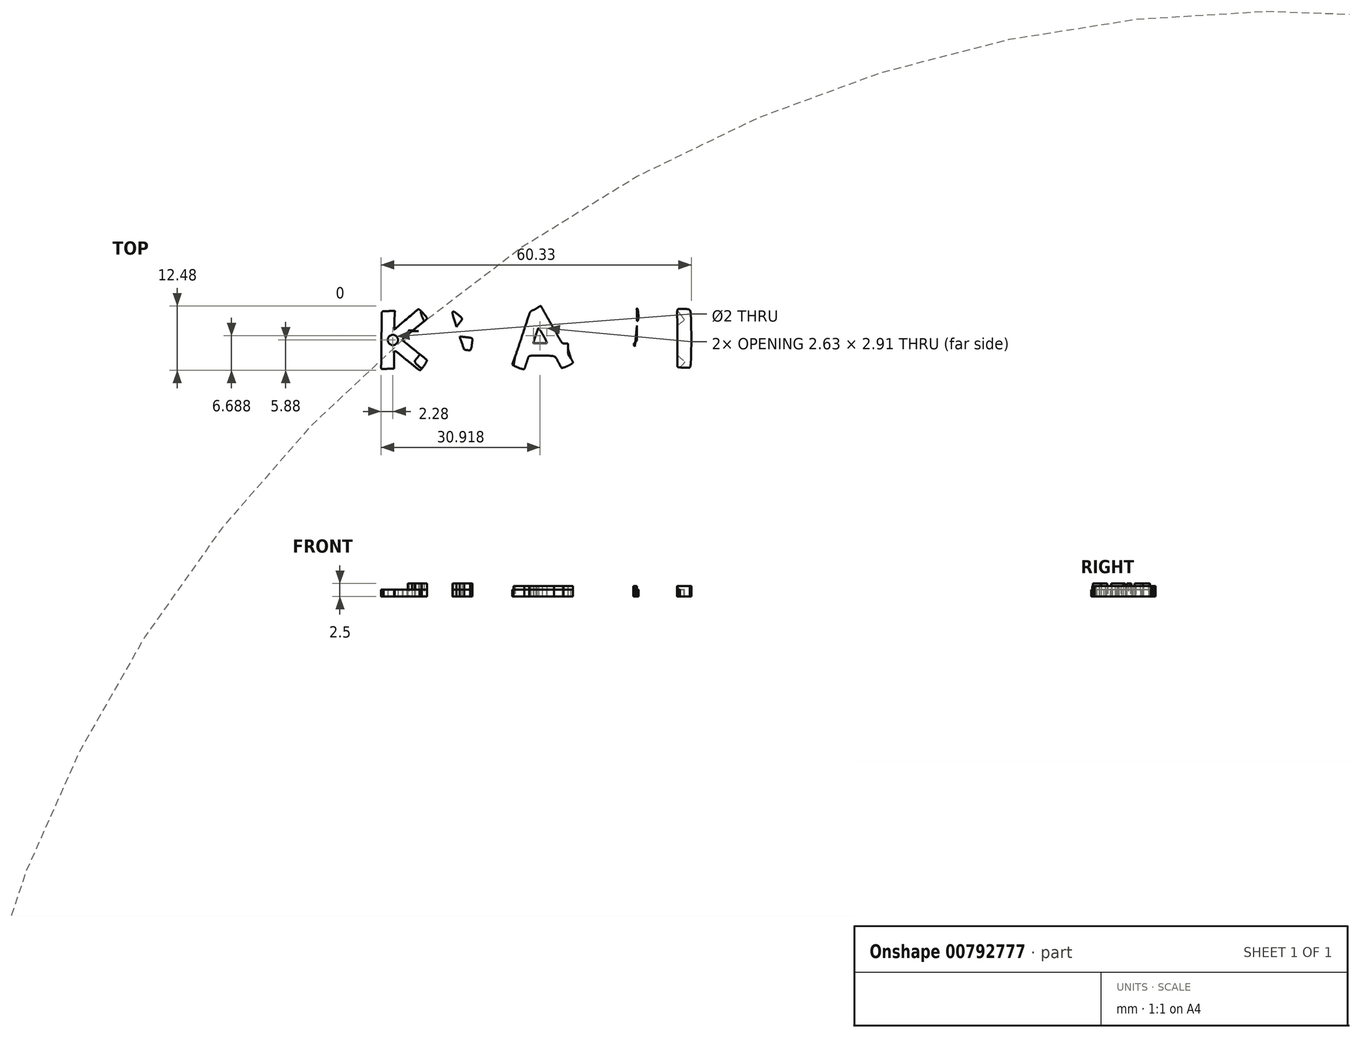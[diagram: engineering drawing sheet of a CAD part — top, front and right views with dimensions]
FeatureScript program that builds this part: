
annotation { "Feature Type Name" : "Feature", "Feature Type Description" : "" }
export const myFeature = defineFeature(function(context is Context, id is Id, definition is map)
    precondition{}
    {
        {
            var Q0;
            Q0=qCreatedBy(makeId("Top.planeOp"),FACE);
            var sketch = newSketch(context, id + "F0", { "sketchPlane" : qUnion([Q0])});
            skFitSpline(sketch, "E0", {"points": [v(29.91, -2.3) * mm, v(29.17, -2.29) * mm, v(28.37, -2.2) * mm, v(28.32, -2.14) * mm]});
            skFitSpline(sketch, "E1", {"points": [v(28.32, -2.14) * mm, v(28.3, -2.1) * mm, v(28.27, -0.7) * mm, v(28.27, 1) * mm]});
            skFitSpline(sketch, "E2", {"points": [v(28.27, 1) * mm, v(28.26, 2.7) * mm, v(28.25, 5.16) * mm, v(28.24, 6.46) * mm]});
            skFitSpline(sketch, "E3", {"points": [v(28.24, 6.46) * mm, v(28.23, 7.77) * mm, v(28.26, 8.88) * mm, v(28.3, 8.93) * mm]});
            skFitSpline(sketch, "E4", {"points": [v(28.3, 8.93) * mm, v(28.4, 9.07) * mm, v(30.48, 9.03) * mm, v(30.66, 8.88) * mm]});
            skFitSpline(sketch, "E5", {"points": [v(30.66, 8.88) * mm, v(30.76, 8.8) * mm, v(30.81, -1.99) * mm, v(30.71, -2.21) * mm]});
            skFitSpline(sketch, "E6", {"points": [v(30.71, -2.21) * mm, v(30.66, -2.33) * mm, v(30.65, -2.33) * mm, v(29.91, -2.3) * mm]});
            skFitSpline(sketch, "E7", {"points": [v(25.4, -0.61) * mm, v(24.06, 0.62) * mm, v(22.96, 1.57) * mm, v(22.92, 1.52) * mm]});
            skFitSpline(sketch, "E8", {"points": [v(22.92, 1.52) * mm, v(22.87, 1.45) * mm, v(22.77, -1.7) * mm, v(22.8, -2) * mm]});
            skFitSpline(sketch, "E9", {"points": [v(22.8, -2) * mm, v(22.82, -2.14) * mm, v(21.16, -2.11) * mm, v(20.64, -1.97) * mm]});
            skFitSpline(sketch, "E10", {"points": [v(20.64, -1.97) * mm, v(20.28, -1.86) * mm, v(20.3, -2) * mm, v(20.33, -0.03) * mm]});
            skFitSpline(sketch, "E11", {"points": [v(20.33, -0.03) * mm, v(20.35, 1.26) * mm, v(20.32, 1.4) * mm, v(19.98, 1.81) * mm]});
            skLineSegment(sketch, "E12", {"start": v(29.91, -2.3) * mm, "end": v(29.91, -2.3) * mm});
            skFitSpline(sketch, "E13", {"points": [v(20.39, 5.86) * mm, v(20.4, 7.46) * mm, v(20.4, 8.81) * mm, v(20.4, 8.86) * mm]});
            skFitSpline(sketch, "E14", {"points": [v(20.4, 8.86) * mm, v(20.36, 9.15) * mm, v(20.5, 9.2) * mm, v(21.46, 9.17) * mm]});
            skFitSpline(sketch, "E15", {"points": [v(21.46, 9.17) * mm, v(22.91, 9.12) * mm, v(22.83, 9.15) * mm, v(22.88, 8.75) * mm]});
            skFitSpline(sketch, "E16", {"points": [v(22.88, 8.75) * mm, v(22.9, 8.56) * mm, v(22.91, 7.68) * mm, v(22.9, 6.81) * mm]});
            skFitSpline(sketch, "E17", {"points": [v(22.9, 6.81) * mm, v(22.89, 5.21) * mm, v(22.9, 5.02) * mm, v(23.08, 5.04) * mm]});
            skFitSpline(sketch, "E18", {"points": [v(23.08, 5.04) * mm, v(23.13, 5.05) * mm, v(24.24, 5.9) * mm, v(25.54, 6.92) * mm]});
            skFitSpline(sketch, "E19", {"points": [v(25.54, 6.92) * mm, v(26.84, 7.94) * mm, v(27.96, 8.81) * mm, v(28.04, 8.85) * mm]});
            skFitSpline(sketch, "E20", {"points": [v(28.04, 8.85) * mm, v(28.13, 8.9) * mm, v(28.36, 8.68) * mm, v(28.83, 8.08) * mm]});
            skFitSpline(sketch, "E21", {"points": [v(28.83, 8.08) * mm, v(29.2, 7.61) * mm, v(29.5, 7.15) * mm, v(29.52, 7.06) * mm]});
            skFitSpline(sketch, "E22", {"points": [v(29.52, 7.06) * mm, v(29.54, 6.92) * mm, v(28.99, 6.44) * mm, v(27.3, 5.1) * mm]});
            skFitSpline(sketch, "E23", {"points": [v(27.3, 5.1) * mm, v(26.05, 4.13) * mm, v(25.05, 3.28) * mm, v(25.05, 3.22) * mm]});
            skFitSpline(sketch, "E24", {"points": [v(25.05, 3.22) * mm, v(25.07, 3.1) * mm, v(25.93, 2.28) * mm, v(28.33, 0.1) * mm]});
            skFitSpline(sketch, "E25", {"points": [v(28.33, 0.1) * mm, v(29.06, -0.56) * mm, v(29.64, -1.14) * mm, v(29.63, -1.18) * mm]});
            skFitSpline(sketch, "E26", {"points": [v(29.63, -1.18) * mm, v(29.58, -1.38) * mm, v(28.09, -2.8) * mm, v(27.9, -2.83) * mm]});
            skFitSpline(sketch, "E27", {"points": [v(27.9, -2.83) * mm, v(27.86, -2.83) * mm, v(26.73, -1.84) * mm, v(25.4, -0.61) * mm]});
            skLineSegment(sketch, "E28", {"start": v(19.98, 1.81) * mm, "end": v(19.69, 2.17) * mm});
            skLineSegment(sketch, "E29", {"start": v(19.69, 2.17) * mm, "end": v(20.03, 2.55) * mm});
            skLineSegment(sketch, "E30", {"start": v(20.03, 2.55) * mm, "end": v(20.37, 2.94) * mm});
            skLineSegment(sketch, "E31", {"start": v(20.37, 2.94) * mm, "end": v(20.39, 5.86) * mm});
            skLineSegment(sketch, "E32", {"start": v(20.39, 5.86) * mm, "end": v(19.98, 1.81) * mm});
            skFitSpline(sketch, "E33", {"points": [v(16.67, -2.5) * mm, v(14.87, -2.5) * mm, v(13.34, -2.48) * mm, v(13.25, -2.46) * mm]});
            skFitSpline(sketch, "E34", {"points": [v(13.25, -2.46) * mm, v(13.14, -2.43) * mm, v(13.1, -2.31) * mm, v(13.1, -1.88) * mm]});
            skFitSpline(sketch, "E35", {"points": [v(13.1, -1.88) * mm, v(13.1, -1.1) * mm, v(13.15, -0.2) * mm, v(13.21, -0.1) * mm]});
            skFitSpline(sketch, "E36", {"points": [v(13.21, -0.1) * mm, v(13.24, -0.06) * mm, v(14.29, -0.03) * mm, v(15.54, -0.03) * mm]});
            skFitSpline(sketch, "E37", {"points": [v(15.54, -0.03) * mm, v(16.8, -0.02) * mm, v(17.96, 0) * mm, v(18.13, 0.02) * mm]});
            skFitSpline(sketch, "E38", {"points": [v(18.13, 0.02) * mm, v(18.49, 0.06) * mm, v(18.5, 0.14) * mm, v(18.4, 1.2) * mm]});
            skFitSpline(sketch, "E39", {"points": [v(16.17, 1.96) * mm, v(14.46, 2) * mm, v(13.95, 2.05) * mm, v(13.84, 2.17) * mm]});
            skFitSpline(sketch, "E40", {"points": [v(13.84, 2.17) * mm, v(13.77, 2.25) * mm, v(13.6, 2.3) * mm, v(13.49, 2.29) * mm]});
            skLineSegment(sketch, "E41", {"start": v(18.4, 1.2) * mm, "end": v(18.35, 1.9) * mm});
            skLineSegment(sketch, "E42", {"start": v(18.35, 1.9) * mm, "end": v(16.17, 1.96) * mm});
            skLineSegment(sketch, "E43", {"start": v(16.17, 1.96) * mm, "end": v(18.4, 1.2) * mm});
            skFitSpline(sketch, "E44", {"points": [v(13.2, 3.42) * mm, v(13.06, 5.28) * mm, v(12.97, 8.73) * mm, v(13.05, 8.85) * mm]});
            skFitSpline(sketch, "E45", {"points": [v(13.05, 8.85) * mm, v(13.1, 8.93) * mm, v(13.67, 8.98) * mm, v(15, 9.03) * mm]});
            skFitSpline(sketch, "E46", {"points": [v(15, 9.03) * mm, v(16.03, 9.07) * mm, v(17.66, 9.13) * mm, v(18.62, 9.17) * mm]});
            skFitSpline(sketch, "E47", {"points": [v(18.62, 9.17) * mm, v(19.58, 9.2) * mm, v(20.38, 9.23) * mm, v(20.4, 9.21) * mm]});
            skFitSpline(sketch, "E48", {"points": [v(20.4, 9.21) * mm, v(20.52, 9.11) * mm, v(20.65, 7) * mm, v(20.53, 6.85) * mm]});
            skFitSpline(sketch, "E49", {"points": [v(20.53, 6.85) * mm, v(20.48, 6.78) * mm, v(19.55, 6.71) * mm, v(18.07, 6.66) * mm]});
            skFitSpline(sketch, "E50", {"points": [v(18.07, 6.66) * mm, v(16.76, 6.6) * mm, v(15.65, 6.53) * mm, v(15.61, 6.48) * mm]});
            skFitSpline(sketch, "E51", {"points": [v(15.61, 6.48) * mm, v(15.58, 6.43) * mm, v(15.57, 5.97) * mm, v(15.6, 5.44) * mm]});
            skFitSpline(sketch, "E52", {"points": [v(15.6, 5.44) * mm, v(15.66, 4.5) * mm, v(15.66, 4.5) * mm, v(15.9, 4.47) * mm]});
            skFitSpline(sketch, "E53", {"points": [v(15.9, 4.47) * mm, v(16.02, 4.45) * mm, v(17.05, 4.42) * mm, v(18.17, 4.4) * mm]});
            skFitSpline(sketch, "E54", {"points": [v(18.17, 4.4) * mm, v(20.74, 4.36) * mm, v(20.65, 4.37) * mm, v(20.68, 4.13) * mm]});
            skFitSpline(sketch, "E55", {"points": [v(20.68, 4.13) * mm, v(20.7, 4.01) * mm, v(20.78, 3.86) * mm, v(20.86, 3.8) * mm]});
            skFitSpline(sketch, "E56", {"points": [v(20.86, 3.8) * mm, v(21.01, 3.65) * mm, v(21.03, 3.36) * mm, v(21.1, 0.44) * mm]});
            skFitSpline(sketch, "E57", {"points": [v(21.1, 0.44) * mm, v(21.12, -0.35) * mm, v(21.14, -1.18) * mm, v(21.15, -1.41) * mm]});
            skFitSpline(sketch, "E58", {"points": [v(21.15, -1.41) * mm, v(21.16, -1.65) * mm, v(21.17, -1.87) * mm, v(21.17, -1.91) * mm]});
            skFitSpline(sketch, "E59", {"points": [v(21.17, -1.91) * mm, v(21.17, -1.95) * mm, v(21.09, -2) * mm, v(21, -2) * mm]});
            skFitSpline(sketch, "E60", {"points": [v(21, -2) * mm, v(20.9, -2.02) * mm, v(20.75, -2.12) * mm, v(20.67, -2.24) * mm]});
            skFitSpline(sketch, "E61", {"points": [v(20.67, -2.24) * mm, v(20.49, -2.5) * mm, v(20.56, -2.5) * mm, v(16.67, -2.5) * mm]});
            skLineSegment(sketch, "E62", {"start": v(13.49, 2.29) * mm, "end": v(13.27, 2.26) * mm});
            skLineSegment(sketch, "E63", {"start": v(13.27, 2.26) * mm, "end": v(13.2, 3.42) * mm});
            skLineSegment(sketch, "E64", {"start": v(13.2, 3.42) * mm, "end": v(13.49, 2.29) * mm});
            skFitSpline(sketch, "E65", {"points": [v(13.77, -2.4) * mm, v(13.7, -2.4) * mm, v(12.32, -2.4) * mm, v(10.73, -2.41) * mm]});
            skFitSpline(sketch, "E66", {"points": [v(10.73, -2.41) * mm, v(6.88, -2.45) * mm, v(7.22, -2.48) * mm, v(7.17, -2.1) * mm]});
            skFitSpline(sketch, "E67", {"points": [v(7.17, -2.1) * mm, v(7.14, -1.87) * mm, v(7.07, -1.75) * mm, v(6.92, -1.7) * mm]});
            skFitSpline(sketch, "E68", {"points": [v(6.92, -1.7) * mm, v(6.75, -1.63) * mm, v(6.72, -1.55) * mm, v(6.72, -1.22) * mm]});
            skFitSpline(sketch, "E69", {"points": [v(6.72, -1.22) * mm, v(6.72, -0.3) * mm, v(6.7, 1.1) * mm, v(6.66, 4.95) * mm]});
            skFitSpline(sketch, "E70", {"points": [v(6.66, 4.95) * mm, v(6.63, 7.18) * mm, v(6.63, 9.05) * mm, v(6.66, 9.11) * mm]});
            skFitSpline(sketch, "E71", {"points": [v(6.66, 9.11) * mm, v(6.74, 9.29) * mm, v(8.8, 9.32) * mm, v(9.01, 9.15) * mm]});
            skFitSpline(sketch, "E72", {"points": [v(9.01, 9.15) * mm, v(9.07, 9.1) * mm, v(9.12, 7.38) * mm, v(9.15, 4.85) * mm]});
            skFitSpline(sketch, "E73", {"points": [v(9.15, 4.85) * mm, v(9.18, 2.53) * mm, v(9.22, 0.5) * mm, v(9.26, 0.35) * mm]});
            skFitSpline(sketch, "E74", {"points": [v(11.56, 0.1) * mm, v(14.38, 0.12) * mm, v(14.22, 0.14) * mm, v(14.26, -0.23) * mm]});
            skFitSpline(sketch, "E75", {"points": [v(14.26, -0.23) * mm, v(14.3, -0.6) * mm, v(14.25, -2.18) * mm, v(14.19, -2.31) * mm]});
            skFitSpline(sketch, "E76", {"points": [v(14.19, -2.31) * mm, v(14.14, -2.41) * mm, v(14.05, -2.43) * mm, v(13.77, -2.4) * mm]});
            skLineSegment(sketch, "E77", {"start": v(9.26, 0.35) * mm, "end": v(9.32, 0.08) * mm});
            skLineSegment(sketch, "E78", {"start": v(9.32, 0.08) * mm, "end": v(11.56, 0.1) * mm});
            skLineSegment(sketch, "E79", {"start": v(11.56, 0.1) * mm, "end": v(9.26, 0.35) * mm});
            skFitSpline(sketch, "E80", {"points": [v(5.56, -2.02) * mm, v(4.89, -0.8) * mm, v(4.47, -0.2) * mm, v(4.24, -0.12) * mm]});
            skFitSpline(sketch, "E81", {"points": [v(4.24, -0.12) * mm, v(3.97, -0.03) * mm, v(-0.42, 0) * mm, v(-0.58, -0.1) * mm]});
            skFitSpline(sketch, "E82", {"points": [v(-0.58, -0.1) * mm, v(-0.64, -0.12) * mm, v(-0.86, -0.67) * mm, v(-1.08, -1.33) * mm]});
            skFitSpline(sketch, "E83", {"points": [v(-1.08, -1.33) * mm, v(-1.3, -1.98) * mm, v(-1.5, -2.54) * mm, v(-1.54, -2.56) * mm]});
            skFitSpline(sketch, "E84", {"points": [v(-1.54, -2.56) * mm, v(-1.61, -2.63) * mm, v(-3.28, -2.06) * mm, v(-3.6, -1.86) * mm]});
            skLineSegment(sketch, "E85", {"start": v(13.77, -2.4) * mm, "end": v(13.77, -2.4) * mm});
            skFitSpline(sketch, "E86", {"points": [v(-3.27, -0.08) * mm, v(-2.96, 0.83) * mm, v(-2.2, 3.1) * mm, v(-1.58, 5) * mm]});
            skFitSpline(sketch, "E87", {"points": [v(-1.58, 5) * mm, v(-0.92, 7) * mm, v(-0.37, 8.5) * mm, v(-0.26, 8.6) * mm]});
            skFitSpline(sketch, "E88", {"points": [v(-0.26, 8.6) * mm, v(-0.15, 8.7) * mm, v(0.05, 8.84) * mm, v(0.2, 8.89) * mm]});
            skFitSpline(sketch, "E89", {"points": [v(0.2, 8.89) * mm, v(0.36, 8.94) * mm, v(0.7, 9.12) * mm, v(0.95, 9.27) * mm]});
            skFitSpline(sketch, "E90", {"points": [v(0.95, 9.27) * mm, v(1.6, 9.66) * mm, v(1.72, 9.66) * mm, v(1.95, 9.27) * mm]});
            skFitSpline(sketch, "E91", {"points": [v(1.95, 9.27) * mm, v(2.06, 9.08) * mm, v(2.95, 7.51) * mm, v(3.93, 5.78) * mm]});
            skFitSpline(sketch, "E92", {"points": [v(3.93, 5.78) * mm, v(4.92, 4.04) * mm, v(5.78, 2.57) * mm, v(5.86, 2.51) * mm]});
            skFitSpline(sketch, "E93", {"points": [v(5.86, 2.51) * mm, v(5.94, 2.45) * mm, v(6.2, 2.4) * mm, v(6.44, 2.4) * mm]});
            skFitSpline(sketch, "E94", {"points": [v(6.44, 2.4) * mm, v(6.68, 2.4) * mm, v(6.9, 2.37) * mm, v(6.94, 2.33) * mm]});
            skFitSpline(sketch, "E95", {"points": [v(6.94, 2.33) * mm, v(6.98, 2.29) * mm, v(7, 1.83) * mm, v(7, 1.32) * mm]});
            skLineSegment(sketch, "E96", {"start": v(-3.6, -1.86) * mm, "end": v(-3.84, -1.72) * mm});
            skLineSegment(sketch, "E97", {"start": v(-3.84, -1.72) * mm, "end": v(-3.27, -0.08) * mm});
            skLineSegment(sketch, "E98", {"start": v(-3.27, -0.08) * mm, "end": v(-3.6, -1.86) * mm});
            skFitSpline(sketch, "E99", {"points": [v(7.49, -0.41) * mm, v(7.75, -0.86) * mm, v(7.95, -1.26) * mm, v(7.92, -1.3) * mm]});
            skFitSpline(sketch, "E100", {"points": [v(7.92, -1.3) * mm, v(7.85, -1.44) * mm, v(6.52, -2.16) * mm, v(6.1, -2.28) * mm]});
            skFitSpline(sketch, "E101", {"points": [v(6.1, -2.28) * mm, v(5.76, -2.39) * mm, v(5.75, -2.38) * mm, v(5.56, -2.02) * mm]});
            skLineSegment(sketch, "E102", {"start": v(7, 1.32) * mm, "end": v(7, 0.4) * mm});
            skLineSegment(sketch, "E103", {"start": v(7, 0.4) * mm, "end": v(7.49, -0.41) * mm});
            skLineSegment(sketch, "E104", {"start": v(7.49, -0.41) * mm, "end": v(7, 1.32) * mm});
            skFitSpline(sketch, "E105", {"points": [v(2.85, 2.58) * mm, v(2.84, 2.72) * mm, v(1.4, 5.2) * mm, v(1.28, 5.29) * mm]});
            skFitSpline(sketch, "E106", {"points": [v(1.28, 5.29) * mm, v(1.2, 5.34) * mm, v(1.03, 4.92) * mm, v(0.73, 4) * mm]});
            skFitSpline(sketch, "E107", {"points": [v(0.73, 4) * mm, v(0.32, 2.77) * mm, v(0.24, 2.48) * mm, v(0.32, 2.46) * mm]});
            skFitSpline(sketch, "E108", {"points": [v(0.32, 2.46) * mm, v(0.34, 2.46) * mm, v(0.75, 2.45) * mm, v(1.25, 2.45) * mm]});
            skFitSpline(sketch, "E109", {"points": [v(1.25, 2.45) * mm, v(2.36, 2.44) * mm, v(2.87, 2.48) * mm, v(2.85, 2.58) * mm]});
            skLineSegment(sketch, "E110", {"start": v(5.56, -2.02) * mm, "end": v(5.56, -2.02) * mm});
            skFitSpline(sketch, "E111", {"points": [v(-4.3, -2.3) * mm, v(-4.55, -2.18) * mm, v(-4.72, -2.17) * mm, v(-5.14, -2.26) * mm]});
            skFitSpline(sketch, "E112", {"points": [v(-5.14, -2.26) * mm, v(-5.74, -2.38) * mm, v(-5.8, -2.34) * mm, v(-5.98, -1.75) * mm]});
            skFitSpline(sketch, "E113", {"points": [v(-5.98, -1.75) * mm, v(-6.62, 0.45) * mm, v(-7.6, 3.54) * mm, v(-7.67, 3.6) * mm]});
            skFitSpline(sketch, "E114", {"points": [v(-7.67, 3.6) * mm, v(-7.73, 3.65) * mm, v(-7.8, 3.54) * mm, v(-7.87, 3.32) * mm]});
            skFitSpline(sketch, "E115", {"points": [v(-7.87, 3.32) * mm, v(-7.92, 3.12) * mm, v(-8.28, 1.9) * mm, v(-8.66, 0.6) * mm]});
            skFitSpline(sketch, "E116", {"points": [v(-8.66, 0.6) * mm, v(-9.04, -0.68) * mm, v(-9.36, -1.82) * mm, v(-9.38, -1.9) * mm]});
            skFitSpline(sketch, "E117", {"points": [v(-9.38, -1.9) * mm, v(-9.42, -2.09) * mm, v(-9.47, -2.1) * mm, v(-10.53, -2.4) * mm]});
            skFitSpline(sketch, "E118", {"points": [v(-10.53, -2.4) * mm, v(-10.91, -2.51) * mm, v(-11.31, -2.64) * mm, v(-11.42, -2.68) * mm]});
            skFitSpline(sketch, "E119", {"points": [v(-11.42, -2.68) * mm, v(-11.58, -2.74) * mm, v(-11.65, -2.71) * mm, v(-11.75, -2.55) * mm]});
            skFitSpline(sketch, "E120", {"points": [v(-11.75, -2.55) * mm, v(-11.93, -2.24) * mm, v(-15.5, 8.4) * mm, v(-15.46, 8.5) * mm]});
            skFitSpline(sketch, "E121", {"points": [v(-15.46, 8.5) * mm, v(-15.44, 8.55) * mm, v(-15.3, 8.6) * mm, v(-15.13, 8.62) * mm]});
            skFitSpline(sketch, "E122", {"points": [v(-15.13, 8.62) * mm, v(-14.97, 8.64) * mm, v(-14.52, 8.77) * mm, v(-14.13, 8.9) * mm]});
            skFitSpline(sketch, "E123", {"points": [v(-14.13, 8.9) * mm, v(-13.73, 9.03) * mm, v(-13.36, 9.13) * mm, v(-13.3, 9.12) * mm]});
            skFitSpline(sketch, "E124", {"points": [v(-13.3, 9.12) * mm, v(-13.22, 9.1) * mm, v(-12.72, 7.75) * mm, v(-12.03, 5.73) * mm]});
            skFitSpline(sketch, "E125", {"points": [v(-12.03, 5.73) * mm, v(-11.4, 3.88) * mm, v(-10.85, 2.36) * mm, v(-10.8, 2.34) * mm]});
            skFitSpline(sketch, "E126", {"points": [v(-10.8, 2.34) * mm, v(-10.7, 2.33) * mm, v(-10.28, 3.68) * mm, v(-9.17, 7.47) * mm]});
            skFitSpline(sketch, "E127", {"points": [v(-9.17, 7.47) * mm, v(-8.76, 8.87) * mm, v(-8.74, 8.9) * mm, v(-8.47, 8.91) * mm]});
            skFitSpline(sketch, "E128", {"points": [v(-8.47, 8.91) * mm, v(-8.32, 8.92) * mm, v(-8.1, 8.9) * mm, v(-8, 8.86) * mm]});
            skFitSpline(sketch, "E129", {"points": [v(-8, 8.86) * mm, v(-7.89, 8.82) * mm, v(-7.5, 8.72) * mm, v(-7.16, 8.64) * mm]});
            skFitSpline(sketch, "E130", {"points": [v(-7.16, 8.64) * mm, v(-6.56, 8.5) * mm, v(-6.52, 8.47) * mm, v(-6.45, 8.18) * mm]});
            skFitSpline(sketch, "E131", {"points": [v(-6.45, 8.18) * mm, v(-6.38, 7.84) * mm, v(-5.6, 5.23) * mm, v(-5.1, 3.64) * mm]});
            skFitSpline(sketch, "E132", {"points": [v(-5.1, 3.64) * mm, v(-4.93, 3.1) * mm, v(-4.79, 2.64) * mm, v(-4.78, 2.62) * mm]});
            skFitSpline(sketch, "E133", {"points": [v(-4.78, 2.62) * mm, v(-4.78, 2.6) * mm, v(-4.74, 2.6) * mm, v(-4.68, 2.6) * mm]});
            skFitSpline(sketch, "E134", {"points": [v(-4.68, 2.6) * mm, v(-4.58, 2.62) * mm, v(-4.26, 3.56) * mm, v(-3.46, 6.23) * mm]});
            skFitSpline(sketch, "E135", {"points": [v(-3.46, 6.23) * mm, v(-2.74, 8.6) * mm, v(-2.57, 9.06) * mm, v(-2.38, 9.08) * mm]});
            skFitSpline(sketch, "E136", {"points": [v(-2.38, 9.08) * mm, v(-2.18, 9.1) * mm, v(-0.35, 8.51) * mm, v(-0.3, 8.4) * mm]});
            skFitSpline(sketch, "E137", {"points": [v(-0.3, 8.4) * mm, v(-0.24, 8.3) * mm, v(-0.9, 6.14) * mm, v(-2.43, 1.41) * mm]});
            skFitSpline(sketch, "E138", {"points": [v(-2.43, 1.41) * mm, v(-3.74, -2.66) * mm, v(-3.7, -2.6) * mm, v(-4.3, -2.3) * mm]});
            skLineSegment(sketch, "E139", {"start": v(2.85, 2.58) * mm, "end": v(2.85, 2.58) * mm});
            skFitSpline(sketch, "E140", {"points": [v(-16.96, -2.82) * mm, v(-17.02, -2.73) * mm, v(-17.36, -2) * mm, v(-17.7, -1.17) * mm]});
            skFitSpline(sketch, "E141", {"points": [v(-17.7, -1.17) * mm, v(-18.06, -0.35) * mm, v(-18.4, 0.36) * mm, v(-18.45, 0.4) * mm]});
            skFitSpline(sketch, "E142", {"points": [v(-18.45, 0.4) * mm, v(-18.52, 0.46) * mm, v(-18.95, -0.04) * mm, v(-19.7, -1.06) * mm]});
            skFitSpline(sketch, "E143", {"points": [v(-19.7, -1.06) * mm, v(-20.34, -1.92) * mm, v(-20.92, -2.62) * mm, v(-20.98, -2.63) * mm]});
            skFitSpline(sketch, "E144", {"points": [v(-20.98, -2.63) * mm, v(-21.15, -2.65) * mm, v(-22.63, -1.48) * mm, v(-22.75, -1.24) * mm]});
            skFitSpline(sketch, "E145", {"points": [v(-22.75, -1.24) * mm, v(-22.83, -1.06) * mm, v(-22.7, -0.84) * mm, v(-21.71, 0.42) * mm]});
            skFitSpline(sketch, "E146", {"points": [v(-21.71, 0.42) * mm, v(-21.04, 1.3) * mm, v(-20.61, 1.93) * mm, v(-20.65, 2) * mm]});
            skFitSpline(sketch, "E147", {"points": [v(-20.65, 2) * mm, v(-20.7, 2.07) * mm, v(-21.4, 2.2) * mm, v(-22.46, 2.31) * mm]});
            skFitSpline(sketch, "E148", {"points": [v(-22.46, 2.31) * mm, v(-23.42, 2.42) * mm, v(-24.26, 2.55) * mm, v(-24.32, 2.61) * mm]});
            skFitSpline(sketch, "E149", {"points": [v(-24.32, 2.61) * mm, v(-24.4, 2.7) * mm, v(-24.4, 2.93) * mm, v(-24.3, 3.49) * mm]});
            skFitSpline(sketch, "E150", {"points": [v(-24.3, 3.49) * mm, v(-24.22, 3.91) * mm, v(-24.16, 4.32) * mm, v(-24.17, 4.4) * mm]});
            skFitSpline(sketch, "E151", {"points": [v(-24.17, 4.4) * mm, v(-24.18, 4.5) * mm, v(-24.13, 4.66) * mm, v(-24.05, 4.78) * mm]});
            skFitSpline(sketch, "E152", {"points": [v(-22.1, 4.77) * mm, v(-21.1, 4.65) * mm, v(-20.27, 4.59) * mm, v(-20.24, 4.63) * mm]});
            skFitSpline(sketch, "E153", {"points": [v(-20.24, 4.63) * mm, v(-20.2, 4.67) * mm, v(-20.5, 5.47) * mm, v(-20.88, 6.41) * mm]});
            skFitSpline(sketch, "E154", {"points": [v(-20.88, 6.41) * mm, v(-21.27, 7.35) * mm, v(-21.6, 8.2) * mm, v(-21.61, 8.3) * mm]});
            skFitSpline(sketch, "E155", {"points": [v(-21.61, 8.3) * mm, v(-21.64, 8.5) * mm, v(-21.55, 8.55) * mm, v(-20.26, 9.06) * mm]});
            skFitSpline(sketch, "E156", {"points": [v(-20.26, 9.06) * mm, v(-19.42, 9.4) * mm, v(-19.43, 9.4) * mm, v(-19, 8.35) * mm]});
            skFitSpline(sketch, "E157", {"points": [v(-19, 8.35) * mm, v(-18.83, 7.94) * mm, v(-18.52, 7.19) * mm, v(-18.31, 6.68) * mm]});
            skFitSpline(sketch, "E158", {"points": [v(-18.31, 6.68) * mm, v(-18.08, 6.13) * mm, v(-17.88, 5.76) * mm, v(-17.81, 5.77) * mm]});
            skFitSpline(sketch, "E159", {"points": [v(-17.81, 5.77) * mm, v(-17.75, 5.77) * mm, v(-17.22, 6.42) * mm, v(-16.65, 7.2) * mm]});
            skFitSpline(sketch, "E160", {"points": [v(-16.65, 7.2) * mm, v(-16.08, 7.97) * mm, v(-15.57, 8.62) * mm, v(-15.52, 8.62) * mm]});
            skFitSpline(sketch, "E161", {"points": [v(-15.52, 8.62) * mm, v(-15.35, 8.64) * mm, v(-13.69, 7.34) * mm, v(-13.67, 7.18) * mm]});
            skFitSpline(sketch, "E162", {"points": [v(-13.67, 7.18) * mm, v(-13.65, 7.1) * mm, v(-14.13, 6.4) * mm, v(-14.71, 5.62) * mm]});
            skFitSpline(sketch, "E163", {"points": [v(-14.71, 5.62) * mm, v(-15.3, 4.84) * mm, v(-15.76, 4.16) * mm, v(-15.73, 4.1) * mm]});
            skFitSpline(sketch, "E164", {"points": [v(-15.73, 4.1) * mm, v(-15.7, 4.04) * mm, v(-14.82, 3.88) * mm, v(-13.77, 3.74) * mm]});
            skFitSpline(sketch, "E165", {"points": [v(-13.77, 3.74) * mm, v(-12.72, 3.6) * mm, v(-11.81, 3.46) * mm, v(-11.75, 3.41) * mm]});
            skFitSpline(sketch, "E166", {"points": [v(-11.75, 3.41) * mm, v(-11.64, 3.33) * mm, v(-11.9, 1.31) * mm, v(-12.04, 1.13) * mm]});
            skFitSpline(sketch, "E167", {"points": [v(-12.04, 1.13) * mm, v(-12.08, 1.08) * mm, v(-12.96, 1.15) * mm, v(-14, 1.28) * mm]});
            skFitSpline(sketch, "E168", {"points": [v(-14, 1.28) * mm, v(-15.38, 1.44) * mm, v(-15.92, 1.48) * mm, v(-15.97, 1.4) * mm]});
            skFitSpline(sketch, "E169", {"points": [v(-15.97, 1.4) * mm, v(-16.03, 1.3) * mm, v(-15.22, -0.78) * mm, v(-14.68, -1.9) * mm]});
            skFitSpline(sketch, "E170", {"points": [v(-14.68, -1.9) * mm, v(-14.6, -2.08) * mm, v(-14.64, -2.12) * mm, v(-15.2, -2.37) * mm]});
            skFitSpline(sketch, "E171", {"points": [v(-15.2, -2.37) * mm, v(-15.54, -2.52) * mm, v(-15.96, -2.69) * mm, v(-16.13, -2.74) * mm]});
            skFitSpline(sketch, "E172", {"points": [v(-16.13, -2.74) * mm, v(-16.3, -2.8) * mm, v(-16.54, -2.86) * mm, v(-16.66, -2.9) * mm]});
            skFitSpline(sketch, "E173", {"points": [v(-16.66, -2.9) * mm, v(-16.79, -2.95) * mm, v(-16.9, -2.91) * mm, v(-16.96, -2.82) * mm]});
            skLineSegment(sketch, "E174", {"start": v(-24.05, 4.78) * mm, "end": v(-23.9, 5) * mm});
            skLineSegment(sketch, "E175", {"start": v(-23.9, 5) * mm, "end": v(-22.1, 4.77) * mm});
            skLineSegment(sketch, "E176", {"start": v(-22.1, 4.77) * mm, "end": v(-24.05, 4.78) * mm});
            skFitSpline(sketch, "E177", {"points": [v(-24.25, -0.94) * mm, v(-25.6, 0.14) * mm, v(-26.62, 0.9) * mm, v(-26.7, 0.87) * mm]});
            skFitSpline(sketch, "E178", {"points": [v(-26.7, 0.87) * mm, v(-26.8, 0.83) * mm, v(-26.84, 0.53) * mm, v(-26.84, -0.41) * mm]});
            skFitSpline(sketch, "E179", {"points": [v(-26.84, -0.41) * mm, v(-26.85, -1.1) * mm, v(-26.85, -1.84) * mm, v(-26.86, -2.07) * mm]});
            skLineSegment(sketch, "E180", {"start": v(-16.96, -2.82) * mm, "end": v(-16.96, -2.82) * mm});
            skFitSpline(sketch, "E181", {"points": [v(-27.69, -2.51) * mm, v(-28.14, -2.53) * mm, v(-28.67, -2.55) * mm, v(-28.86, -2.57) * mm]});
            skFitSpline(sketch, "E182", {"points": [v(-28.86, -2.57) * mm, v(-29.06, -2.59) * mm, v(-29.25, -2.57) * mm, v(-29.29, -2.54) * mm]});
            skFitSpline(sketch, "E183", {"points": [v(-29.29, -2.54) * mm, v(-29.33, -2.51) * mm, v(-29.36, -1.79) * mm, v(-29.35, -0.94) * mm]});
            skFitSpline(sketch, "E184", {"points": [v(-29.35, -0.94) * mm, v(-29.34, -0.09) * mm, v(-29.32, 2.37) * mm, v(-29.3, 4.52) * mm]});
            skFitSpline(sketch, "E185", {"points": [v(-29.3, 4.52) * mm, v(-29.28, 6.74) * mm, v(-29.22, 8.48) * mm, v(-29.16, 8.55) * mm]});
            skFitSpline(sketch, "E186", {"points": [v(-29.16, 8.55) * mm, v(-29.09, 8.65) * mm, v(-28.84, 8.68) * mm, v(-28.11, 8.7) * mm]});
            skFitSpline(sketch, "E187", {"points": [v(-28.11, 8.7) * mm, v(-26.88, 8.73) * mm, v(-26.7, 8.68) * mm, v(-26.72, 8.33) * mm]});
            skFitSpline(sketch, "E188", {"points": [v(-26.72, 8.33) * mm, v(-26.73, 8.2) * mm, v(-26.75, 7.6) * mm, v(-26.76, 7.02) * mm]});
            skFitSpline(sketch, "E189", {"points": [v(-26.76, 7.02) * mm, v(-26.77, 6.45) * mm, v(-26.78, 5.83) * mm, v(-26.79, 5.66) * mm]});
            skFitSpline(sketch, "E190", {"points": [v(-26.79, 5.66) * mm, v(-26.8, 5.11) * mm, v(-26.77, 5.14) * mm, v(-23.64, 7.81) * mm]});
            skFitSpline(sketch, "E191", {"points": [v(-23.64, 7.81) * mm, v(-22.84, 8.5) * mm, v(-22.13, 9.04) * mm, v(-22.07, 9.03) * mm]});
            skFitSpline(sketch, "E192", {"points": [v(-22.07, 9.03) * mm, v(-21.94, 8.99) * mm, v(-20.55, 7.51) * mm, v(-20.5, 7.35) * mm]});
            skFitSpline(sketch, "E193", {"points": [v(-20.5, 7.35) * mm, v(-20.45, 7.24) * mm, v(-21.56, 6.27) * mm, v(-24.36, 3.95) * mm]});
            skFitSpline(sketch, "E194", {"points": [v(-24.36, 3.95) * mm, v(-24.97, 3.43) * mm, v(-25.19, 3.2) * mm, v(-25.15, 3.08) * mm]});
            skFitSpline(sketch, "E195", {"points": [v(-25.15, 3.08) * mm, v(-25.13, 2.99) * mm, v(-24.07, 2.08) * mm, v(-22.8, 1.06) * mm]});
            skFitSpline(sketch, "E196", {"points": [v(-22.8, 1.06) * mm, v(-21.53, 0.05) * mm, v(-20.5, -0.81) * mm, v(-20.49, -0.85) * mm]});
            skFitSpline(sketch, "E197", {"points": [v(-20.49, -0.85) * mm, v(-20.47, -1) * mm, v(-21.71, -2.77) * mm, v(-21.85, -2.78) * mm]});
            skFitSpline(sketch, "E198", {"points": [v(-21.85, -2.78) * mm, v(-21.9, -2.8) * mm, v(-22.98, -1.96) * mm, v(-24.25, -0.94) * mm]});
            skLineSegment(sketch, "E199", {"start": v(-26.86, -2.07) * mm, "end": v(-26.87, -2.49) * mm});
            skLineSegment(sketch, "E200", {"start": v(-26.87, -2.49) * mm, "end": v(-27.69, -2.51) * mm});
            skLineSegment(sketch, "E201", {"start": v(-27.69, -2.51) * mm, "end": v(-26.86, -2.07) * mm});
            skPoint(sketch, "E202", {"position": v(-27.08, 3.08) * mm});
            skSolve(sketch);
        }
        {
            var Q0;
            {var subQ1=sQuery(id+"F0.wireOp",EDGE,"E151");Q0=makeQuery(id+"F0.imprint","IMPRINT",FACE,{"disambiguationData":[TD([[makeQuery(id+"F0.imprint","IMPRINT",EDGE,{"derivedFrom":subQ1}),1.0]])]});}
            var Q1;
            {var subQ0=sQuery(id+"F0.wireOp",EDGE,"E174");Q1=makeQuery(id+"F0.imprint","IMPRINT",FACE,{"disambiguationData":[TD([[makeQuery(id+"F0.imprint","IMPRINT",EDGE,{"derivedFrom":subQ0}),-1.0]])]});}
            var Q2;
            {var subQ0=sQuery(id+"F0.wireOp",EDGE,"E151");Q2=makeQuery(id+"F0.imprint","IMPRINT",FACE,{"disambiguationData":[TD([[makeQuery(id+"F0.imprint","IMPRINT",EDGE,{"derivedFrom":subQ0}),-1.0]])]});}
            var Q3;
            {var subQ0=sQuery(id+"F0.wireOp",EDGE,"E155");var subQ1=sQuery(id+"F0.wireOp",EDGE,"E154");var subQ2=makeQuery(id+"F0.imprint","INTERSECT",VERTEX,{"derivedFrom":[subQ1,subQ0]});Q3=makeQuery(id+"F0.imprint","IMPRINT",FACE,{"disambiguationData":[TD([[makeQuery(id+"F0.imprint","IMPRINT",EDGE,{"disambiguationData":[TD([[subQ2,1.0]])],"derivedFrom":subQ1}),-1.0]])]});}
            var Q4;
            {var subQ0=sQuery(id+"F0.wireOp",EDGE,"E145");var subQ1=sQuery(id+"F0.wireOp",EDGE,"E144");var subQ2=makeQuery(id+"F0.imprint","INTERSECT",VERTEX,{"derivedFrom":[subQ1,subQ0]});Q4=makeQuery(id+"F0.imprint","IMPRINT",FACE,{"disambiguationData":[TD([[makeQuery(id+"F0.imprint","IMPRINT",EDGE,{"disambiguationData":[TD([[subQ2,1.0]])],"derivedFrom":subQ1}),-1.0]])]});}
            var Q5;
            {var subQ0=sQuery(id+"F0.wireOp",EDGE,"E121");var subQ1=sQuery(id+"F0.wireOp",EDGE,"E120");var subQ2=makeQuery(id+"F0.imprint","INTERSECT",VERTEX,{"derivedFrom":[subQ1,subQ0]});Q5=makeQuery(id+"F0.imprint","IMPRINT",FACE,{"disambiguationData":[TD([[makeQuery(id+"F0.imprint","IMPRINT",EDGE,{"disambiguationData":[TD([[subQ2,1.0]])],"derivedFrom":subQ1}),-1.0]])]});}
            var Q6;
            {var subQ13=sQuery(id+"F0.wireOp",EDGE,"E86");Q6=makeQuery(id+"F0.imprint","IMPRINT",FACE,{"disambiguationData":[TD([[makeQuery(id+"F0.imprint","IMPRINT",EDGE,{"derivedFrom":subQ13}),1.0]])]});}
            var Q7;
            {var subQ1=sQuery(id+"F0.wireOp",EDGE,"E165");Q7=makeQuery(id+"F0.imprint","IMPRINT",FACE,{"disambiguationData":[TD([[makeQuery(id+"F0.imprint","IMPRINT",EDGE,{"derivedFrom":subQ1}),-1.0]])]});}
            var Q8;
            {var subQ0=sQuery(id+"F0.wireOp",EDGE,"E21");Q8=makeQuery(id+"F0.imprint","IMPRINT",FACE,{"disambiguationData":[TD([[makeQuery(id+"F0.imprint","IMPRINT",EDGE,{"derivedFrom":subQ0}),-1.0]])]});}
            var Q9;
            {var subQ0=sQuery(id+"F0.wireOp",EDGE,"E25");Q9=makeQuery(id+"F0.imprint","IMPRINT",FACE,{"disambiguationData":[TD([[makeQuery(id+"F0.imprint","IMPRINT",EDGE,{"derivedFrom":subQ0}),-1.0]])]});}
            var Q10;
            {var subQ0=sQuery(id+"F0.wireOp",EDGE,"E35");Q10=makeQuery(id+"F0.imprint","IMPRINT",FACE,{"disambiguationData":[TD([[makeQuery(id+"F0.imprint","IMPRINT",EDGE,{"derivedFrom":subQ0}),1.0]])]});}
            var Q11;
            Q11=makeQuery(id+"F0.imprint","IMPRINT",FACE,{"disambiguationData":[TD([[makeQuery(id+"F0.imprint","IMPRINT",EDGE,{"derivedFrom":sQuery(id+"F0.wireOp",EDGE,"E102")}),1.0]])]});
            var Q12;
            {var subQ9=sQuery(id+"F0.wireOp",EDGE,"E10");Q12=makeQuery(id+"F0.imprint","IMPRINT",FACE,{"disambiguationData":[TD([[makeQuery(id+"F0.imprint","IMPRINT",EDGE,{"derivedFrom":subQ9}),-1.0]])]});}
            var Q13;
            {var subQ0=sQuery(id+"F0.wireOp",EDGE,"E28");Q13=makeQuery(id+"F0.imprint","IMPRINT",FACE,{"disambiguationData":[TD([[makeQuery(id+"F0.imprint","IMPRINT",EDGE,{"derivedFrom":subQ0}),-1.0]])]});}
            var Q14;
            Q14=makeQuery(id+"F0.imprint","IMPRINT",FACE,{"disambiguationData":[TD([[makeQuery(id+"F0.imprint","IMPRINT",EDGE,{"derivedFrom":sQuery(id+"F0.wireOp",EDGE,"E7")}),-1.0]])]});
            var Q15;
            {var subQ0=sQuery(id+"F0.wireOp",EDGE,"E14");var subQ1=sQuery(id+"F0.wireOp",EDGE,"E13");var subQ2=makeQuery(id+"F0.imprint","INTERSECT",VERTEX,{"derivedFrom":[subQ1,subQ0]});Q15=makeQuery(id+"F0.imprint","IMPRINT",FACE,{"disambiguationData":[TD([[makeQuery(id+"F0.imprint","IMPRINT",EDGE,{"disambiguationData":[TD([[subQ2,1.0]])],"derivedFrom":subQ1}),-1.0]])]});}
            var Q16;
            {var subQ5=sQuery(id+"F0.wireOp",EDGE,"E35");Q16=makeQuery(id+"F0.imprint","IMPRINT",FACE,{"disambiguationData":[TD([[makeQuery(id+"F0.imprint","IMPRINT",EDGE,{"derivedFrom":subQ5}),-1.0]])]});}
            var Q17;
            {var subQ1=sQuery(id+"F0.wireOp",EDGE,"E68");Q17=makeQuery(id+"F0.imprint","IMPRINT",FACE,{"disambiguationData":[TD([[makeQuery(id+"F0.imprint","IMPRINT",EDGE,{"derivedFrom":subQ1}),-1.0]])]});}
            var Q18;
            {var subQ1=sQuery(id+"F0.wireOp",EDGE,"E86");Q18=makeQuery(id+"F0.imprint","IMPRINT",FACE,{"disambiguationData":[TD([[makeQuery(id+"F0.imprint","IMPRINT",EDGE,{"derivedFrom":subQ1}),-1.0]])]});}
            var Q19;
            Q19=makeQuery(id+"F0.imprint","IMPRINT",FACE,{"disambiguationData":[TD([[makeQuery(id+"F0.imprint","IMPRINT",EDGE,{"derivedFrom":sQuery(id+"F0.wireOp",EDGE,"E96")}),-1.0]])]});
            var Q20;
            Q20=makeQuery(id+"F0.imprint","IMPRINT",FACE,{"disambiguationData":[TD([[makeQuery(id+"F0.imprint","IMPRINT",EDGE,{"derivedFrom":sQuery(id+"F0.wireOp",EDGE,"E199")}),-1.0]])]});
            extrude(context, id + "F1", {"entities" : qUnion([Q0, Q1, Q2, Q3, Q4, Q5, Q6, Q7, Q8, Q9, Q10, Q11, Q12, Q13, Q14, Q15, Q16, Q17, Q18, Q19, Q20]), "depth" : 1.3 * mm, "offsetDistance" : 25 * mm});
        }
        {
            var Q0;
            Q0=makeQuery(id+"F0.imprint","IMPRINT",FACE,{"disambiguationData":[TD([[makeQuery(id+"F0.imprint","IMPRINT",EDGE,{"derivedFrom":sQuery(id+"F0.wireOp",EDGE,"E140")}),-1.0]])]});
            var Q1;
            {var subQ1=sQuery(id+"F0.wireOp",EDGE,"E175");var subQ3=sQuery(id+"F0.wireOp",EDGE,"E193");var subQ4=makeQuery(id+"F0.imprint","INTERSECT",VERTEX,{"derivedFrom":[subQ1,subQ3]});Q1=makeQuery(id+"F0.imprint","IMPRINT",FACE,{"disambiguationData":[TD([[makeQuery(id+"F0.imprint","IMPRINT",EDGE,{"disambiguationData":[TD([[subQ4,-1.0]])],"derivedFrom":subQ3}),1.0]])]});}
            var Q2;
            {var subQ0=sQuery(id+"F0.wireOp",EDGE,"E151");Q2=makeQuery(id+"F0.imprint","IMPRINT",FACE,{"disambiguationData":[TD([[makeQuery(id+"F0.imprint","IMPRINT",EDGE,{"derivedFrom":subQ0}),-1.0]])]});}
            var Q3;
            {var subQ0=sQuery(id+"F0.wireOp",EDGE,"E174");Q3=makeQuery(id+"F0.imprint","IMPRINT",FACE,{"disambiguationData":[TD([[makeQuery(id+"F0.imprint","IMPRINT",EDGE,{"derivedFrom":subQ0}),-1.0]])]});}
            var Q4;
            {var subQ0=sQuery(id+"F0.wireOp",EDGE,"E121");var subQ1=sQuery(id+"F0.wireOp",EDGE,"E120");var subQ2=makeQuery(id+"F0.imprint","INTERSECT",VERTEX,{"derivedFrom":[subQ1,subQ0]});Q4=makeQuery(id+"F0.imprint","IMPRINT",FACE,{"disambiguationData":[TD([[makeQuery(id+"F0.imprint","IMPRINT",EDGE,{"disambiguationData":[TD([[subQ2,1.0]])],"derivedFrom":subQ1}),-1.0]])]});}
            var Q5;
            {var subQ1=sQuery(id+"F0.wireOp",EDGE,"E165");Q5=makeQuery(id+"F0.imprint","IMPRINT",FACE,{"disambiguationData":[TD([[makeQuery(id+"F0.imprint","IMPRINT",EDGE,{"derivedFrom":subQ1}),-1.0]])]});}
            var Q6;
            {var subQ0=sQuery(id+"F0.wireOp",EDGE,"E145");var subQ1=sQuery(id+"F0.wireOp",EDGE,"E144");var subQ2=makeQuery(id+"F0.imprint","INTERSECT",VERTEX,{"derivedFrom":[subQ1,subQ0]});Q6=makeQuery(id+"F0.imprint","IMPRINT",FACE,{"disambiguationData":[TD([[makeQuery(id+"F0.imprint","IMPRINT",EDGE,{"disambiguationData":[TD([[subQ2,1.0]])],"derivedFrom":subQ1}),-1.0]])]});}
            var Q7;
            {var subQ0=sQuery(id+"F0.wireOp",EDGE,"E155");var subQ1=sQuery(id+"F0.wireOp",EDGE,"E154");var subQ2=makeQuery(id+"F0.imprint","INTERSECT",VERTEX,{"derivedFrom":[subQ1,subQ0]});Q7=makeQuery(id+"F0.imprint","IMPRINT",FACE,{"disambiguationData":[TD([[makeQuery(id+"F0.imprint","IMPRINT",EDGE,{"disambiguationData":[TD([[subQ2,1.0]])],"derivedFrom":subQ1}),-1.0]])]});}
            extrude(context, id + "F2", {"entities" : qUnion([Q0, Q1, Q2, Q3, Q4, Q5, Q6, Q7]), "depth" : 2.5 * mm, "offsetDistance" : 25 * mm});
        }
        {
            var Q0;
            {var subQ4=sQuery(id+"F0.wireOp",EDGE,"E68");Q0=makeQuery(id+"F0.imprint","IMPRINT",FACE,{"disambiguationData":[TD([[makeQuery(id+"F0.imprint","IMPRINT",EDGE,{"derivedFrom":subQ4}),1.0]])]});}
            var Q1;
            {var subQ20=sQuery(id+"F0.wireOp",EDGE,"E10");Q1=makeQuery(id+"F0.imprint","IMPRINT",FACE,{"disambiguationData":[TD([[makeQuery(id+"F0.imprint","IMPRINT",EDGE,{"derivedFrom":subQ20}),1.0]])]});}
            var Q2;
            {var subQ13=sQuery(id+"F0.wireOp",EDGE,"E4");Q2=makeQuery(id+"F0.imprint","IMPRINT",FACE,{"disambiguationData":[TD([[makeQuery(id+"F0.imprint","IMPRINT",EDGE,{"derivedFrom":subQ13}),-1.0]])]});}
            var Q3;
            {var subQ0=sQuery(id+"F0.wireOp",EDGE,"E31");var subQ1=sQuery(id+"F0.wireOp",EDGE,"E30");var subQ2=makeQuery(id+"F0.imprint","INTERSECT",VERTEX,{"derivedFrom":[subQ1,subQ0]});Q3=makeQuery(id+"F0.imprint","IMPRINT",FACE,{"disambiguationData":[TD([[makeQuery(id+"F0.imprint","IMPRINT",EDGE,{"disambiguationData":[TD([[subQ2,1.0]])],"derivedFrom":subQ1}),1.0]])]});}
            var Q4;
            {var subQ1=sQuery(id+"F0.wireOp",EDGE,"E68");Q4=makeQuery(id+"F0.imprint","IMPRINT",FACE,{"disambiguationData":[TD([[makeQuery(id+"F0.imprint","IMPRINT",EDGE,{"derivedFrom":subQ1}),-1.0]])]});}
            var Q5;
            {var subQ5=sQuery(id+"F0.wireOp",EDGE,"E35");Q5=makeQuery(id+"F0.imprint","IMPRINT",FACE,{"disambiguationData":[TD([[makeQuery(id+"F0.imprint","IMPRINT",EDGE,{"derivedFrom":subQ5}),-1.0]])]});}
            var Q6;
            {var subQ9=sQuery(id+"F0.wireOp",EDGE,"E10");Q6=makeQuery(id+"F0.imprint","IMPRINT",FACE,{"disambiguationData":[TD([[makeQuery(id+"F0.imprint","IMPRINT",EDGE,{"derivedFrom":subQ9}),-1.0]])]});}
            var Q7;
            {var subQ0=sQuery(id+"F0.wireOp",EDGE,"E28");Q7=makeQuery(id+"F0.imprint","IMPRINT",FACE,{"disambiguationData":[TD([[makeQuery(id+"F0.imprint","IMPRINT",EDGE,{"derivedFrom":subQ0}),-1.0]])]});}
            var Q8;
            {var subQ0=sQuery(id+"F0.wireOp",EDGE,"E21");Q8=makeQuery(id+"F0.imprint","IMPRINT",FACE,{"disambiguationData":[TD([[makeQuery(id+"F0.imprint","IMPRINT",EDGE,{"derivedFrom":subQ0}),-1.0]])]});}
            var Q9;
            {var subQ0=sQuery(id+"F0.wireOp",EDGE,"E25");Q9=makeQuery(id+"F0.imprint","IMPRINT",FACE,{"disambiguationData":[TD([[makeQuery(id+"F0.imprint","IMPRINT",EDGE,{"derivedFrom":subQ0}),-1.0]])]});}
            extrude(context, id + "F3", {"entities" : qUnion([Q0, Q1, Q2, Q3, Q4, Q5, Q6, Q7, Q8, Q9]), "depth" : 2 * mm, "offsetDistance" : 25 * mm});
        }
        {
            var Q0;
            Q0=sQuery(id+"F0.wireOp",VERTEX,"98df06a5-b47a-4582-a184-941af1bcfc49");
            var Q1;
            Q1=sQuery(id+"F0.wireOp",VERTEX,"E202");
            var Q2;
            Q2=makeQuery(id+"F1.opExtrude","SWEPT_BODY",BODY,{"disambiguationData":[OSD([sQuery(id+"F0.wireOp",EDGE,"E177"),sQuery(id+"F0.wireOp",EDGE,"E178"),sQuery(id+"F0.wireOp",EDGE,"E179"),sQuery(id+"F0.wireOp",EDGE,"E181"),sQuery(id+"F0.wireOp",EDGE,"E182"),sQuery(id+"F0.wireOp",EDGE,"E183"),sQuery(id+"F0.wireOp",EDGE,"E184"),sQuery(id+"F0.wireOp",EDGE,"E185"),sQuery(id+"F0.wireOp",EDGE,"E186"),sQuery(id+"F0.wireOp",EDGE,"E187"),sQuery(id+"F0.wireOp",EDGE,"E188"),sQuery(id+"F0.wireOp",EDGE,"E189"),sQuery(id+"F0.wireOp",EDGE,"E190"),sQuery(id+"F0.wireOp",EDGE,"E191"),sQuery(id+"F0.wireOp",EDGE,"E192"),sQuery(id+"F0.wireOp",EDGE,"E193"),sQuery(id+"F0.wireOp",EDGE,"E194"),sQuery(id+"F0.wireOp",EDGE,"E195"),sQuery(id+"F0.wireOp",EDGE,"E196"),sQuery(id+"F0.wireOp",EDGE,"E197"),sQuery(id+"F0.wireOp",EDGE,"E198"),sQuery(id+"F0.wireOp",EDGE,"E201")])]});
            hole(context, id + "F4", {"style" : HoleStyle.SIMPLE, "endStyle" : HoleEndStyle.THROUGH, "oppositeDirection" : true, "holeDiameter" : 2 * mm, "majorDiameter" : 5 * mm, "isTappedThrough" : true, "tappedDepth" : 12 * mm, "tapClearance" : 3, "locations" : qUnion([Q0, Q1]), "scope" : qUnion([Q2])});
        }
    });
